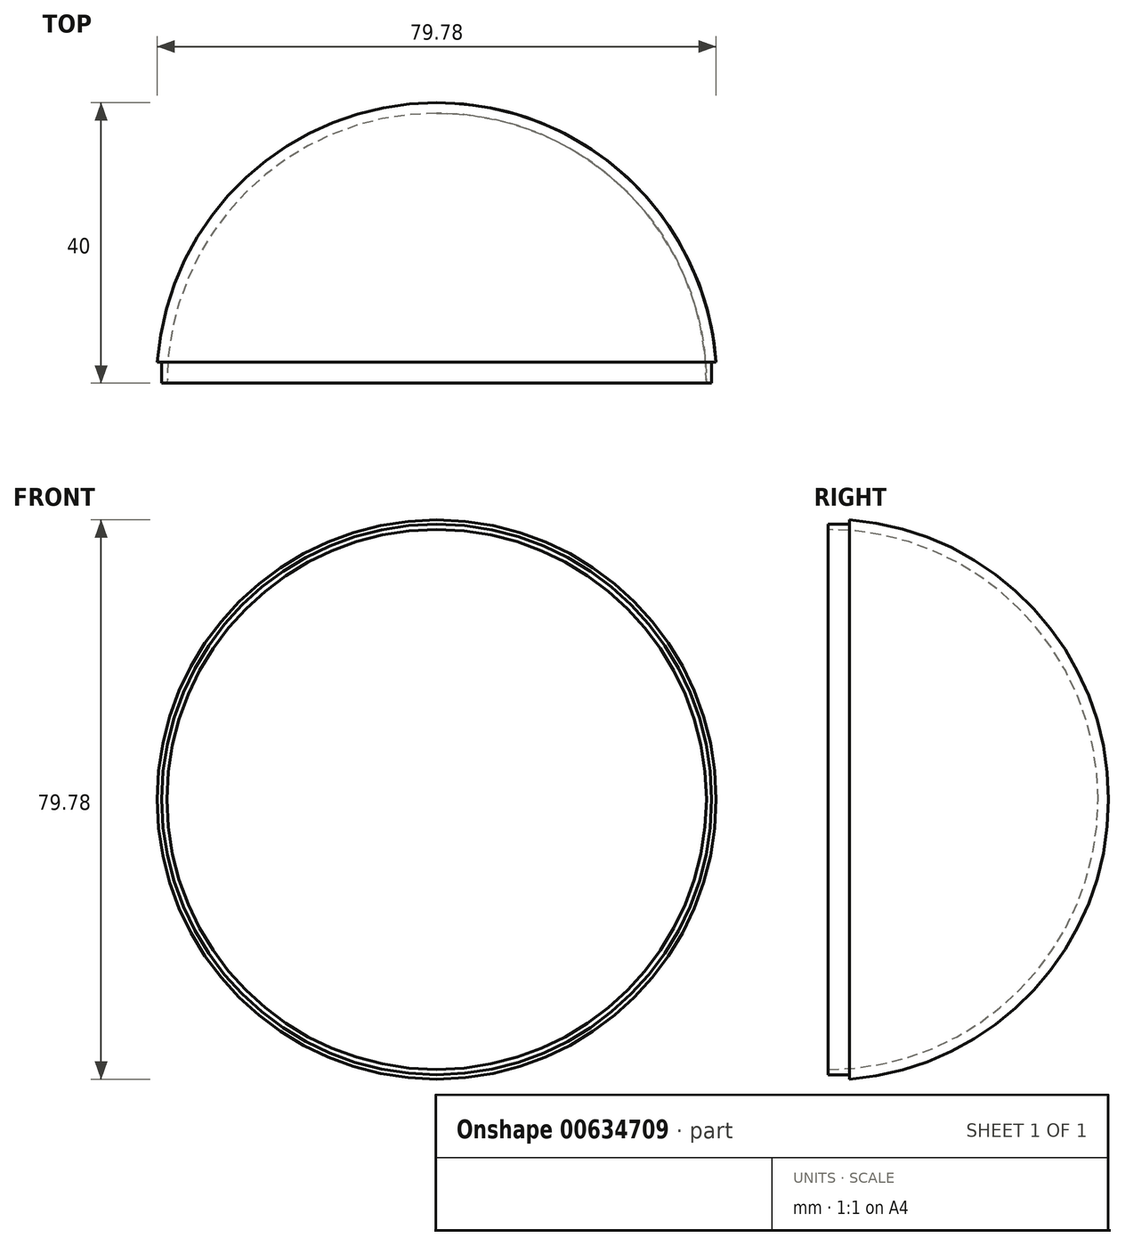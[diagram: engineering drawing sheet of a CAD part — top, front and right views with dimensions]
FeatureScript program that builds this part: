
annotation { "Feature Type Name" : "Feature", "Feature Type Description" : "" }
export const myFeature = defineFeature(function(context is Context, id is Id, definition is map)
    precondition{}
    {
        {
            var Q0;
            Q0=qCreatedBy(makeId("Top.planeOp"),FACE);
            var sketch = newSketch(context, id + "F0", { "sketchPlane" : qUnion([Q0])});
            skArc(sketch, "E0", {"start": v(39.89, 3) * mm, "mid": v(27.2, 29.33) * mm, "end": v(0, 40) * mm});
            skArc(sketch, "E1.0", {"start": v(38.5, 0) * mm, "mid": v(27.22, 27.22) * mm, "end": v(0, 38.5) * mm});
            skLineSegment(sketch, "E2", {"start": v(38.5, 0) * mm, "end": v(40, 0) * mm});
            skLineSegment(sketch, "E3", {"start": v(39.25, 0) * mm, "end": v(39.25, 3) * mm});
            skLineSegment(sketch, "E4", {"start": v(39.25, 3) * mm, "end": v(39.89, 3) * mm});
            skLineSegment(sketch, "E5.trimOffspring", {"start": v(40, 0) * mm, "end": v(54.32, 0) * mm, "construction": true});
            skLineSegment(sketch, "E6", {"start": v(0, 40) * mm, "end": v(0, 38.5) * mm});
            skLineSegment(sketch, "E7.trimOffspring", {"start": v(-38.5, 0) * mm, "end": v(39.25, 0) * mm, "construction": true});
            skPoint(sketch, "E8.end.orphan", {"position": v(-40, 0) * mm});
            skPoint(sketch, "E8.start.orphan", {"position": v(-55.87, 0) * mm});
            skLineSegment(sketch, "E9", {"start": v(0, 0) * mm, "end": v(0, 48.07) * mm, "construction": true});
            skSolve(sketch);
        }
        {
            var Q0;
            Q0=makeQuery(id+"F0.imprint","IMPRINT",FACE,{"disambiguationData":[TD([[makeQuery(id+"F0.imprint","IMPRINT",EDGE,{"derivedFrom":sQuery(id+"F0.wireOp",EDGE,"E0")}),1.0]])]});
            var Q1;
            Q1=sQuery(id+"F0.wireOp",EDGE,"E9");
            revolve(context, id + "F1", {"entities" : qUnion([Q0]), "axis" : qUnion([Q1]), "revolveType" : RevolveType.FULL});
        }
    });
